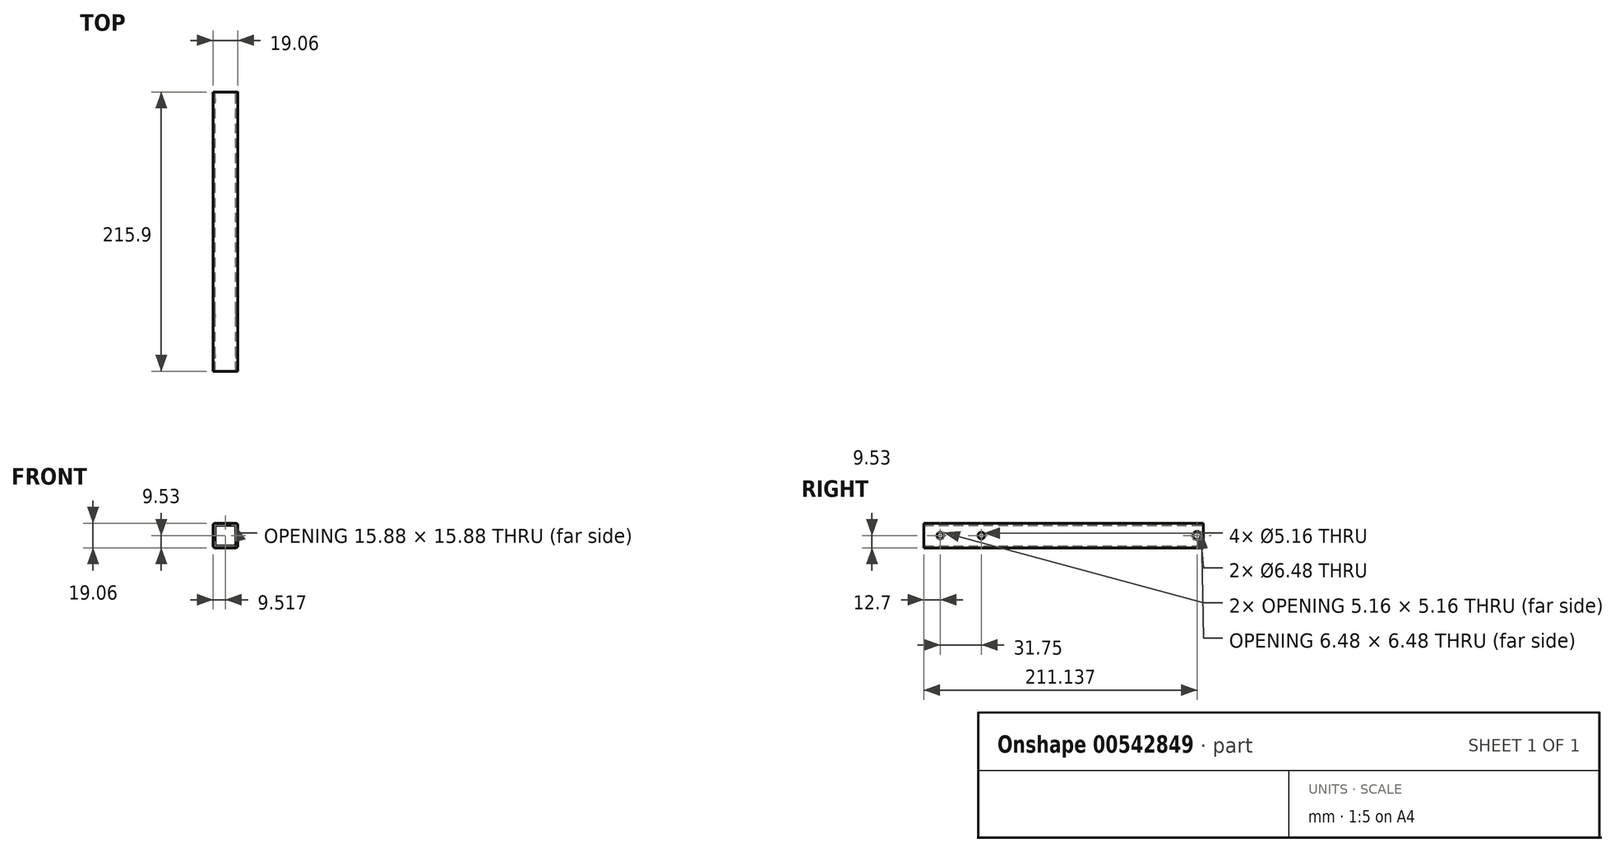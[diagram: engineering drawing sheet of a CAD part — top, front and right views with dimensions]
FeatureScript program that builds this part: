
annotation { "Feature Type Name" : "Feature", "Feature Type Description" : "" }
export const myFeature = defineFeature(function(context is Context, id is Id, definition is map)
    precondition{}
    {
        {
            var Q0;
            Q0=qCreatedBy(makeId("Front.planeOp"),FACE);
            var sketch = newSketch(context, id + "F0", { "sketchPlane" : qUnion([Q0])});
            skLineSegment(sketch, "E0.bottom", {"start": v(-9.53, 9.53) * mm, "end": v(9.53, 9.53) * mm});
            skLineSegment(sketch, "E0.top", {"start": v(-9.53, -9.53) * mm, "end": v(9.53, -9.53) * mm});
            skLineSegment(sketch, "E0.left", {"start": v(-9.53, 9.53) * mm, "end": v(-9.53, -9.53) * mm});
            skLineSegment(sketch, "E0.right", {"start": v(9.53, 9.53) * mm, "end": v(9.53, -9.53) * mm});
            skPoint(sketch, "E1", {"position": v(-9.53, 0) * mm});
            skPoint(sketch, "E2", {"position": v(9.53, 0) * mm});
            skPoint(sketch, "E3", {"position": v(0, -9.53) * mm});
            skPoint(sketch, "E4", {"position": v(0, 9.53) * mm});
            skLineSegment(sketch, "E5.bottom", {"start": v(-7.95, 7.94) * mm, "end": v(7.92, 7.94) * mm});
            skLineSegment(sketch, "E5.top", {"start": v(-7.95, -7.94) * mm, "end": v(7.92, -7.94) * mm});
            skLineSegment(sketch, "E5.left", {"start": v(-7.95, 7.94) * mm, "end": v(-7.95, -7.94) * mm});
            skLineSegment(sketch, "E5.right", {"start": v(7.92, 7.94) * mm, "end": v(7.92, -7.94) * mm});
            skSolve(sketch);
        }
        {
            var Q0;
            Q0=qSketchRegion(id+"F0",true);
            extrude(context, id + "F1", {"entities" : qUnion([Q0]), "depth" : 215.9 * mm, "offsetDistance" : 25.4 * mm, "symmetric" : true});
        }
        {
            var Q0;
            Q0=makeQuery(id+"F1.opExtrude","SWEPT_EDGE",EDGE,{"disambiguationData":[OSD([sQuery(id+"F0.wireOp",EDGE,"E0.bottom"),sQuery(id+"F0.wireOp",EDGE,"E0.left")])]});
            var Q1;
            Q1=makeQuery(id+"F1.opExtrude","SWEPT_EDGE",EDGE,{"disambiguationData":[OSD([sQuery(id+"F0.wireOp",EDGE,"E0.top"),sQuery(id+"F0.wireOp",EDGE,"E0.left")])]});
            var Q2;
            Q2=makeQuery(id+"F1.opExtrude","SWEPT_EDGE",EDGE,{"disambiguationData":[OSD([sQuery(id+"F0.wireOp",EDGE,"E0.top"),sQuery(id+"F0.wireOp",EDGE,"E0.right")])]});
            var Q3;
            Q3=makeQuery(id+"F1.opExtrude","SWEPT_EDGE",EDGE,{"disambiguationData":[OSD([sQuery(id+"F0.wireOp",EDGE,"E0.bottom"),sQuery(id+"F0.wireOp",EDGE,"E0.right")])]});
            fillet(context, id + "F2", {"entities" : qUnion([Q0, Q1, Q2, Q3]), "radius" : 1.59 * mm, "tangentPropagation" : true, "allowEdgeOverflow" : false});
        }
        {
            var Q0;
            Q0=makeQuery(id+"F1.opExtrude","SWEPT_EDGE",EDGE,{"disambiguationData":[OSD([sQuery(id+"F0.wireOp",EDGE,"E5.bottom"),sQuery(id+"F0.wireOp",EDGE,"E5.left")])]});
            var Q1;
            Q1=makeQuery(id+"F1.opExtrude","SWEPT_EDGE",EDGE,{"disambiguationData":[OSD([sQuery(id+"F0.wireOp",EDGE,"E5.top"),sQuery(id+"F0.wireOp",EDGE,"E5.left")])]});
            var Q2;
            Q2=makeQuery(id+"F1.opExtrude","SWEPT_EDGE",EDGE,{"disambiguationData":[OSD([sQuery(id+"F0.wireOp",EDGE,"E5.bottom"),sQuery(id+"F0.wireOp",EDGE,"E5.right")])]});
            var Q3;
            Q3=makeQuery(id+"F1.opExtrude","SWEPT_EDGE",EDGE,{"disambiguationData":[OSD([sQuery(id+"F0.wireOp",EDGE,"E5.top"),sQuery(id+"F0.wireOp",EDGE,"E5.right")])]});
            fillet(context, id + "F3", {"entities" : qUnion([Q0, Q1, Q2, Q3]), "radius" : 1.59 * mm, "tangentPropagation" : true, "allowEdgeOverflow" : false});
        }
        {
            var Q0;
            Q0=makeQuery(id+"F1.opExtrude","SWEPT_FACE",FACE,{"disambiguationData":[OSD([sQuery(id+"F0.wireOp",EDGE,"E0.left")])]});
            var sketch = newSketch(context, id + "F4", { "sketchPlane" : qUnion([Q0])});
            skCircle(sketch, "E6", {"center": v(-103.19, 0) * mm, "radius": 3.24 * mm});
            skCircle(sketch, "E7", {"center": v(63.5, 0) * mm, "radius": 2.58 * mm});
            skPoint(sketch, "E7.centerSnap0", {"position": v(-107.95, 0) * mm});
            skCircle(sketch, "E8", {"center": v(95.25, 0) * mm, "radius": 2.58 * mm});
            skSolve(sketch);
        }
        {
            var Q0;
            Q0=makeQuery(id+"F4.imprint","IMPRINT",FACE,{"disambiguationData":[TD([[makeQuery(id+"F4.imprint","IMPRINT",EDGE,{"derivedFrom":sQuery(id+"F4.wireOp",EDGE,"E6")}),1.0]])]});
            var Q1;
            Q1=makeQuery(id+"F4.imprint","IMPRINT",FACE,{"disambiguationData":[TD([[makeQuery(id+"F4.imprint","IMPRINT",EDGE,{"derivedFrom":sQuery(id+"F4.wireOp",EDGE,"E7")}),1.0]])]});
            var Q2;
            Q2=makeQuery(id+"F4.imprint","IMPRINT",FACE,{"disambiguationData":[TD([[makeQuery(id+"F4.imprint","IMPRINT",EDGE,{"derivedFrom":sQuery(id+"F4.wireOp",EDGE,"E8")}),1.0]])]});
            var Q3;
            Q3=sQuery(id+"F4.wireOp",EDGE,"E6");
            var Q4;
            Q4=sQuery(id+"F4.wireOp",EDGE,"E7");
            var Q5;
            Q5=sQuery(id+"F4.wireOp",EDGE,"E8");
            extrude(context, id + "F5", {"entities" : qUnion([Q0, Q1, Q2]), "operationType" : NewBodyOperationType.REMOVE, "surfaceEntities" : qUnion([Q3, Q4, Q5]), "oppositeDirection" : true, "depth" : 19.05 * mm, "offsetDistance" : 25.4 * mm});
        }
        {
            var Q0;
            Q0=makeQuery(id+"F1.opExtrude","CAP_FACE",FACE,{"disambiguationData":[OSD([sQuery(id+"F0.wireOp",EDGE,"E0.bottom"),sQuery(id+"F0.wireOp",EDGE,"E0.top"),sQuery(id+"F0.wireOp",EDGE,"E0.left"),sQuery(id+"F0.wireOp",EDGE,"E0.right"),sQuery(id+"F0.wireOp",EDGE,"E5.bottom"),sQuery(id+"F0.wireOp",EDGE,"E5.top"),sQuery(id+"F0.wireOp",EDGE,"E5.left"),sQuery(id+"F0.wireOp",EDGE,"E5.right")])],"isStart":false});
            extrude(context, id + "F6", {"entities" : qUnion([Q0]), "operationType" : NewBodyOperationType.REMOVE, "oppositeDirection" : true, "depth" : 1 / 203.2 * mm, "offsetDistance" : 25.4 * mm});
        }
    });
